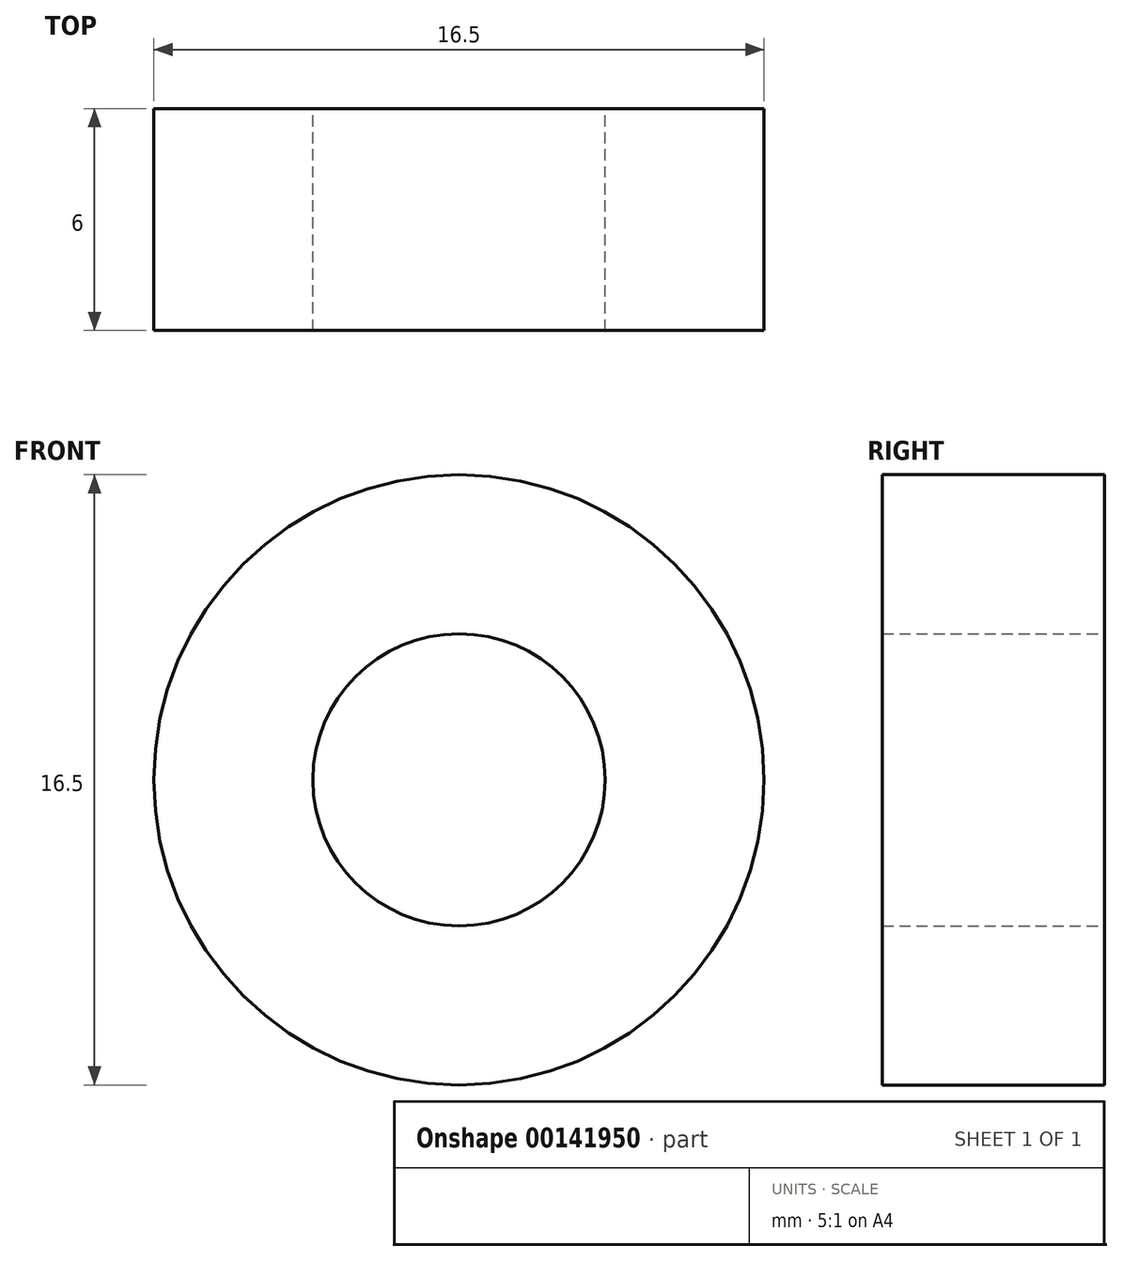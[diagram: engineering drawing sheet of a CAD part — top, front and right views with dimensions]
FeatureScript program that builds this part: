
annotation { "Feature Type Name" : "Feature", "Feature Type Description" : "" }
export const myFeature = defineFeature(function(context is Context, id is Id, definition is map)
    precondition{}
    {
        {
            var Q0;
            Q0=qCreatedBy(makeId("Front.planeOp"),FACE);
            var sketch = newSketch(context, id + "F0", { "sketchPlane" : qUnion([Q0])});
            skCircle(sketch, "E0", {"center": v(0, 0) * mm, "radius": 3.95 * mm});
            skCircle(sketch, "E1", {"center": v(0, 0) * mm, "radius": 8.25 * mm});
            skSolve(sketch);
        }
        {
            var Q0;
            Q0=makeQuery(id+"F0.imprint","IMPRINT",FACE,{"disambiguationData":[TD([[makeQuery(id+"F0.imprint","IMPRINT",EDGE,{"derivedFrom":sQuery(id+"F0.wireOp",EDGE,"E0")}),-1.0]])]});
            extrude(context, id + "F1", {"entities" : qUnion([Q0]), "depth" : 6 * mm, "offsetDistance" : 25 * mm});
        }
    });
